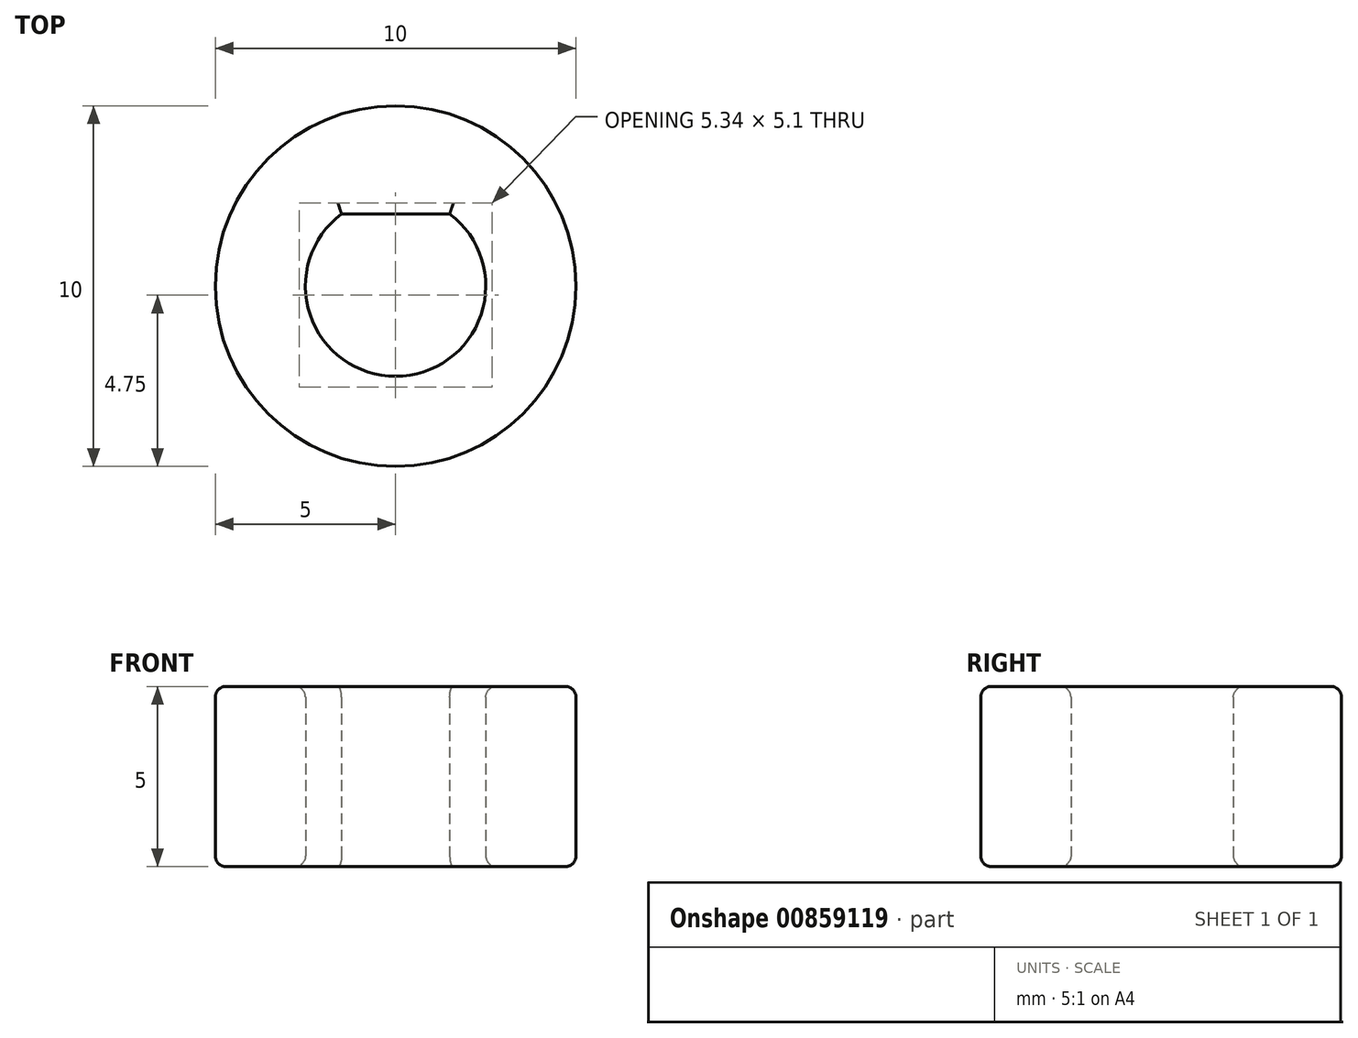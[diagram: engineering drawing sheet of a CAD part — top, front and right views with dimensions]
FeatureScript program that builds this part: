
annotation { "Feature Type Name" : "Feature", "Feature Type Description" : "" }
export const myFeature = defineFeature(function(context is Context, id is Id, definition is map)
    precondition{}
    {
        {
            var Q0;
            Q0=qCreatedBy(makeId("Top.planeOp"),FACE);
            var sketch = newSketch(context, id + "F0", { "sketchPlane" : qUnion([Q0])});
            skCircle(sketch, "E0", {"center": v(0, 0) * mm, "radius": 2.5 * mm});
            skCircle(sketch, "E1", {"center": v(0, 0) * mm, "radius": 5 * mm});
            skArc(sketch, "E2", {"start": v(-0.99, 25.16) * mm, "mid": v(0, 26) * mm, "end": v(0.99, 25.16) * mm});
            skLineSegment(sketch, "E3", {"start": v(-1.5, 2) * mm, "end": v(1.5, 2) * mm});
            skLineSegment(sketch, "E4", {"start": v(-4.94, 0.8) * mm, "end": v(-0.99, 25.16) * mm});
            skLineSegment(sketch, "E5", {"start": v(4.94, 0.8) * mm, "end": v(0.99, 25.16) * mm});
            skSolve(sketch);
        }
        {
            var Q0;
            Q0=makeQuery(id+"F0.imprint","IMPRINT",FACE,{"disambiguationData":[TD([[makeQuery(id+"F0.imprint","IMPRINT",EDGE,{"derivedFrom":sQuery(id+"F0.wireOp",EDGE,"E2")}),-1.0]])]});
            var Q1;
            {var subQ0=sQuery(id+"F0.wireOp",EDGE,"E3");var subQ1=sQuery(id+"F0.wireOp",EDGE,"E0");var subQ2=makeQuery(id+"F0.imprint","INTERSECT",VERTEX,{"disambiguationData":[OD(0.0)],"derivedFrom":[subQ1,subQ0]});Q1=makeQuery(id+"F0.imprint","IMPRINT",FACE,{"disambiguationData":[TD([[makeQuery(id+"F0.imprint","IMPRINT",EDGE,{"disambiguationData":[TD([[subQ2,1.0]])],"derivedFrom":subQ1}),-1.0]])]});}
            var Q2;
            {var subQ0=sQuery(id+"F0.wireOp",EDGE,"E3");Q2=makeQuery(id+"F0.imprint","IMPRINT",FACE,{"disambiguationData":[TD([[makeQuery(id+"F0.imprint","IMPRINT",EDGE,{"derivedFrom":subQ0}),1.0]])]});}
            extrude(context, id + "F1", {"entities" : qUnion([Q0, Q1, Q2]), "depth" : 5 * mm, "offsetDistance" : 25 * mm});
        }
        {
            var Q0;
            Q0=makeQuery(id+"F1.opExtrude","CAP_FACE",FACE,{"disambiguationData":[OSD([sQuery(id+"F0.wireOp",EDGE,"E0"),sQuery(id+"F0.wireOp",EDGE,"E1"),sQuery(id+"F0.wireOp",EDGE,"E2"),sQuery(id+"F0.wireOp",EDGE,"E3"),sQuery(id+"F0.wireOp",EDGE,"E4"),sQuery(id+"F0.wireOp",EDGE,"E5")])],"isStart":false});
            var Q1;
            Q1=makeQuery(id+"F1.opExtrude","CAP_FACE",FACE,{"disambiguationData":[OSD([sQuery(id+"F0.wireOp",EDGE,"E0"),sQuery(id+"F0.wireOp",EDGE,"E1"),sQuery(id+"F0.wireOp",EDGE,"E2"),sQuery(id+"F0.wireOp",EDGE,"E3"),sQuery(id+"F0.wireOp",EDGE,"E4"),sQuery(id+"F0.wireOp",EDGE,"E5")])],"isStart":true});
            fillet(context, id + "F2", {"entities" : qUnion([Q0, Q1]), "radius" : 0.3 * mm, "tangentPropagation" : true, "allowEdgeOverflow" : false});
        }
    });
